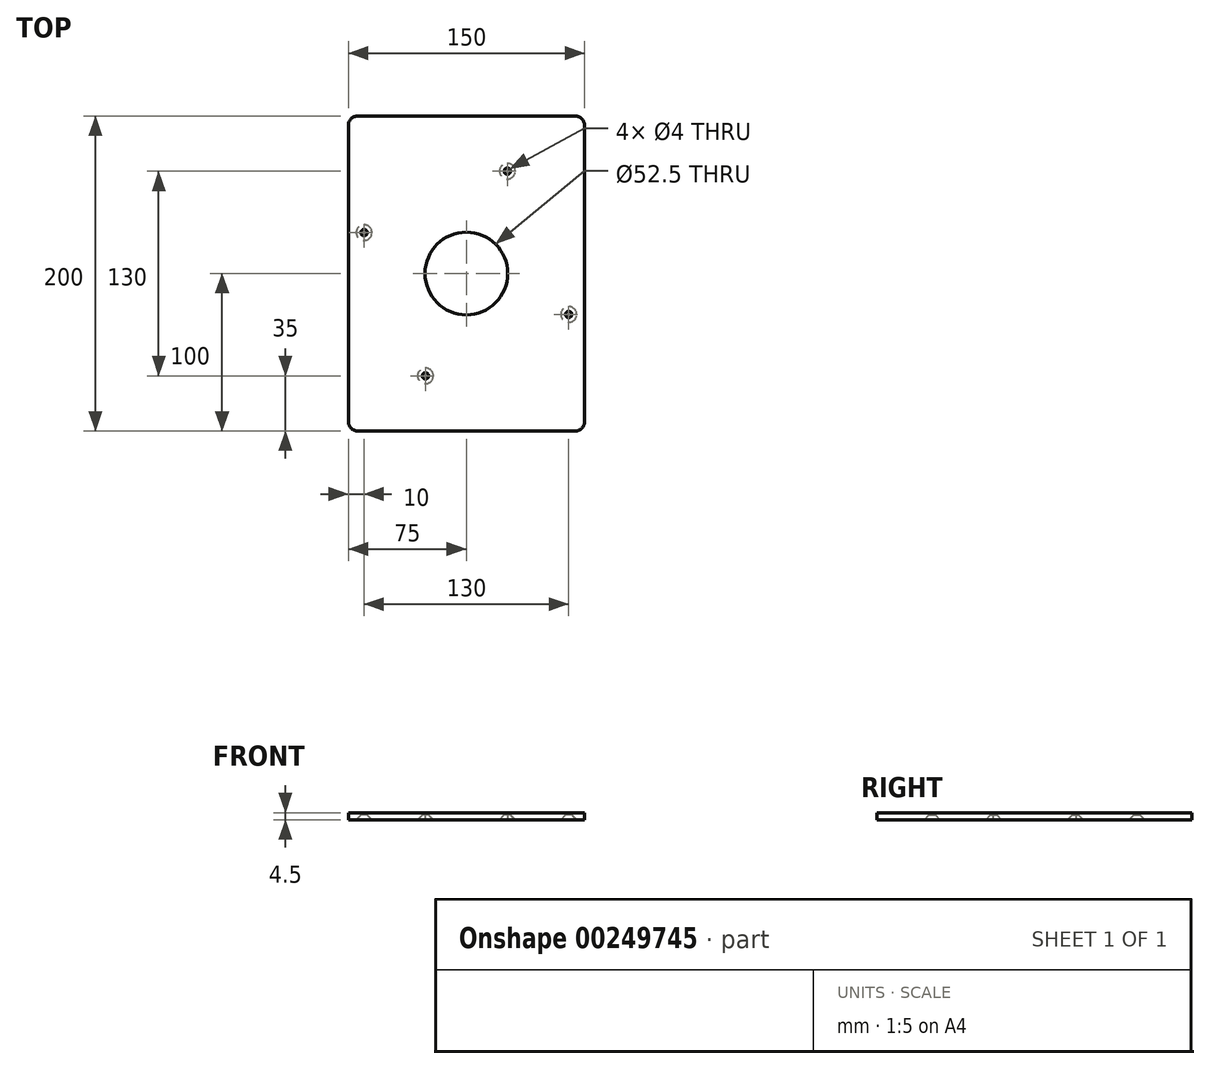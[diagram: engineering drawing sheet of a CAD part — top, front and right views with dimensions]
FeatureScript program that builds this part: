
annotation { "Feature Type Name" : "Feature", "Feature Type Description" : "" }
export const myFeature = defineFeature(function(context is Context, id is Id, definition is map)
    precondition{}
    {
        {
            var Q0;
            Q0=qCreatedBy(makeId("Top.planeOp"),FACE);
            var sketch = newSketch(context, id + "F0", { "sketchPlane" : qUnion([Q0])});
            skCircle(sketch, "E0", {"center": v(0, 0) * mm, "radius": 75 * mm, "construction": true});
            skCircle(sketch, "E1", {"center": v(65, -26) * mm, "radius": 2 * mm});
            skCircle(sketch, "E2", {"center": v(26, 65) * mm, "radius": 2 * mm});
            skCircle(sketch, "E3", {"center": v(-65, 26) * mm, "radius": 2 * mm});
            skCircle(sketch, "E4", {"center": v(-26, -65) * mm, "radius": 2 * mm});
            skLineSegment(sketch, "E5.bottom", {"start": v(-69, 100) * mm, "end": v(69, 100) * mm});
            skLineSegment(sketch, "E5.top", {"start": v(-69, -100) * mm, "end": v(69, -100) * mm});
            skLineSegment(sketch, "E5.left", {"start": v(-75, 94) * mm, "end": v(-75, -94) * mm});
            skLineSegment(sketch, "E5.right", {"start": v(75, 94) * mm, "end": v(75, -94) * mm});
            skPoint(sketch, "E6.visualSharp", {"position": v(-75, 100) * mm});
            skArc(sketch, "E6.filletArc", {"start": v(-69, 100) * mm, "mid": v(-73.24, 98.24) * mm, "end": v(-75, 94) * mm});
            skPoint(sketch, "E7.visualSharp", {"position": v(75, 100) * mm});
            skArc(sketch, "E7.filletArc", {"start": v(75, 94) * mm, "mid": v(73.24, 98.24) * mm, "end": v(69, 100) * mm});
            skPoint(sketch, "E8.visualSharp", {"position": v(75, -100) * mm});
            skArc(sketch, "E8.filletArc", {"start": v(69, -100) * mm, "mid": v(73.24, -98.24) * mm, "end": v(75, -94) * mm});
            skPoint(sketch, "E9.visualSharp", {"position": v(-75, -100) * mm});
            skArc(sketch, "E9.filletArc", {"start": v(-75, -94) * mm, "mid": v(-73.24, -98.24) * mm, "end": v(-69, -100) * mm});
            skCircle(sketch, "E10", {"center": v(0, 0) * mm, "radius": 26.25 * mm});
            skSolve(sketch);
        }
        {
            var Q0;
            Q0=makeQuery(id+"F0.imprint","IMPRINT",FACE,{"disambiguationData":[TD([[makeQuery(id+"F0.imprint","IMPRINT",EDGE,{"derivedFrom":sQuery(id+"F0.wireOp",EDGE,"E1")}),-1.0]])]});
            extrude(context, id + "F1", {"entities" : qUnion([Q0]), "depth" : 4.5 * mm});
        }
        {
            var Q0;
            Q0=makeQuery(id+"F1.opExtrude","CAP_EDGE",EDGE,{"disambiguationData":[OSD([sQuery(id+"F0.wireOp",EDGE,"E3")])],"isStart":true});
            var Q1;
            Q1=makeQuery(id+"F1.opExtrude","CAP_EDGE",EDGE,{"disambiguationData":[OSD([sQuery(id+"F0.wireOp",EDGE,"E4")])],"isStart":true});
            var Q2;
            Q2=makeQuery(id+"F1.opExtrude","CAP_EDGE",EDGE,{"disambiguationData":[OSD([sQuery(id+"F0.wireOp",EDGE,"E1")])],"isStart":true});
            var Q3;
            Q3=makeQuery(id+"F1.opExtrude","CAP_EDGE",EDGE,{"disambiguationData":[OSD([sQuery(id+"F0.wireOp",EDGE,"E2")])],"isStart":true});
            chamfer(context, id + "F2", {"entities" : qUnion([Q0, Q1, Q2, Q3]), "width" : 3 * mm, "tangentPropagation" : true});
        }
    });
